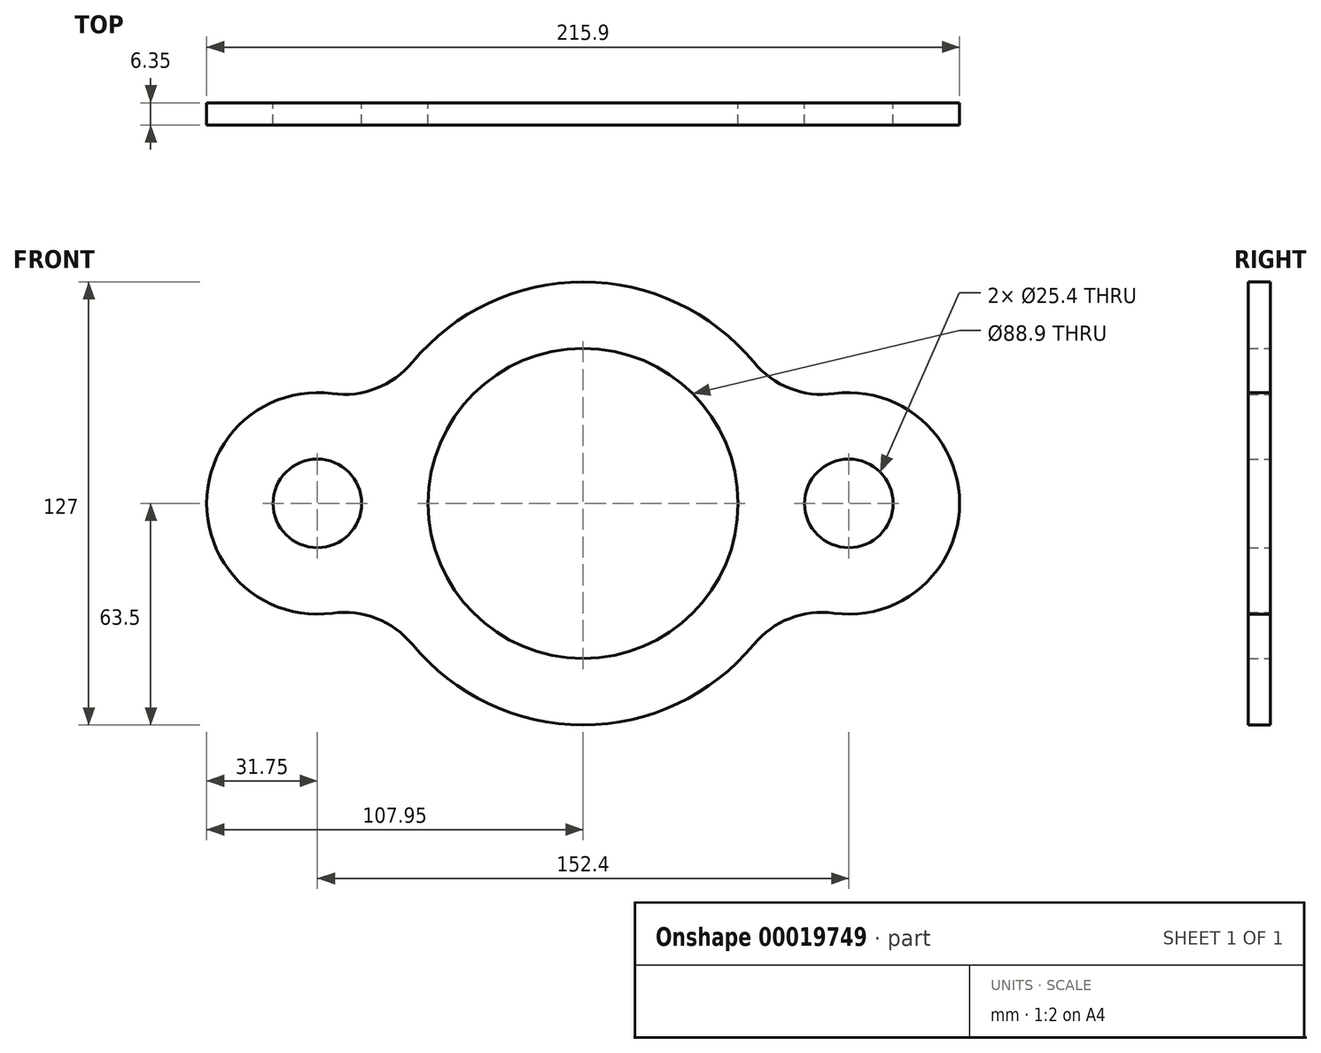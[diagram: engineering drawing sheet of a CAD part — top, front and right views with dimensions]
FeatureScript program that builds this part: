
annotation { "Feature Type Name" : "Feature", "Feature Type Description" : "" }
export const myFeature = defineFeature(function(context is Context, id is Id, definition is map)
    precondition{}
    {
        {
            var Q0;
            Q0=qCreatedBy(makeId("Front.planeOp"),FACE);
            var sketch = newSketch(context, id + "F0", { "sketchPlane" : qUnion([Q0])});
            skCircle(sketch, "E0", {"center": v(0, 0) * mm, "radius": 44.45 * mm});
            skArc(sketch, "E1", {"start": v(-48.95, -40.45) * mm, "mid": v(0, -63.5) * mm, "end": v(48.95, -40.45) * mm});
            skCircle(sketch, "E2", {"center": v(-76.2, 0) * mm, "radius": 12.7 * mm});
            skCircle(sketch, "E3", {"center": v(76.2, 0) * mm, "radius": 12.7 * mm});
            skArc(sketch, "E4", {"start": v(-71.94, 31.46) * mm, "mid": v(-107.95, 0) * mm, "end": v(-71.94, -31.46) * mm});
            skArc(sketch, "E5", {"start": v(71.94, -31.46) * mm, "mid": v(107.95, 0) * mm, "end": v(71.94, 31.46) * mm});
            skArc(sketch, "E6.trimOffspring", {"start": v(48.95, 40.45) * mm, "mid": v(0, 63.5) * mm, "end": v(-48.95, 40.45) * mm});
            skPoint(sketch, "E7.visualSharp", {"position": v(57.94, 25.98) * mm});
            skArc(sketch, "E7.filletArc", {"start": v(48.95, 40.45) * mm, "mid": v(59.28, 32.98) * mm, "end": v(71.94, 31.46) * mm});
            skPoint(sketch, "E8.visualSharp", {"position": v(57.94, -25.98) * mm});
            skArc(sketch, "E8.filletArc", {"start": v(71.94, -31.46) * mm, "mid": v(59.28, -32.98) * mm, "end": v(48.95, -40.45) * mm});
            skPoint(sketch, "E9.visualSharp", {"position": v(-57.94, -25.98) * mm});
            skArc(sketch, "E9.filletArc", {"start": v(-48.95, -40.45) * mm, "mid": v(-59.28, -32.98) * mm, "end": v(-71.94, -31.46) * mm});
            skPoint(sketch, "E10.visualSharp", {"position": v(-57.94, 25.98) * mm});
            skArc(sketch, "E10.filletArc", {"start": v(-71.94, 31.46) * mm, "mid": v(-59.28, 32.98) * mm, "end": v(-48.95, 40.45) * mm});
            skSolve(sketch);
        }
        {
            var Q0;
            Q0=makeQuery(id+"F0.imprint","IMPRINT",FACE,{"disambiguationData":[TD([[makeQuery(id+"F0.imprint","IMPRINT",EDGE,{"derivedFrom":sQuery(id+"F0.wireOp",EDGE,"E0")}),-1.0]])]});
            extrude(context, id + "F1", {"entities" : qUnion([Q0]), "depth" : 6.35 * mm});
        }
    });
